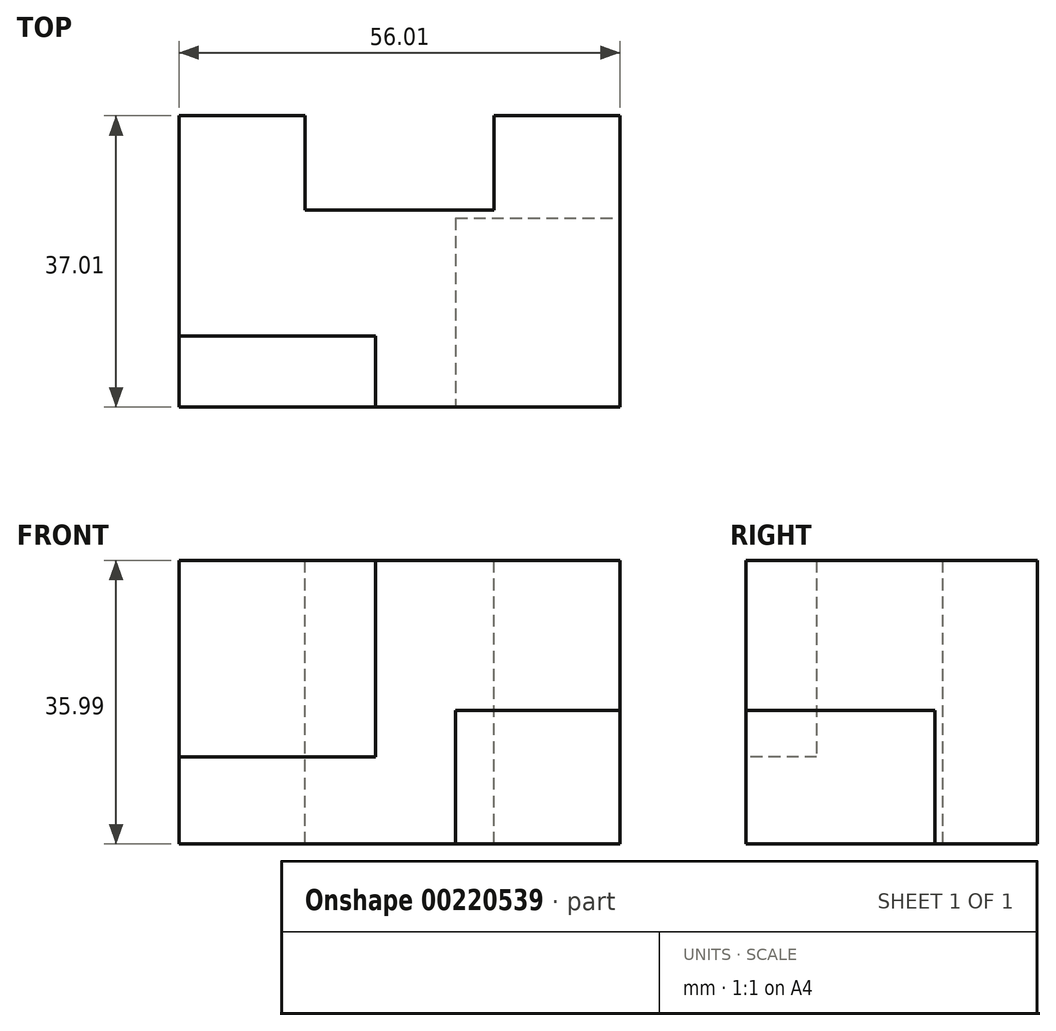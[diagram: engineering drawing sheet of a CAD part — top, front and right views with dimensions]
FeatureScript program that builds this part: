
annotation { "Feature Type Name" : "Feature", "Feature Type Description" : "" }
export const myFeature = defineFeature(function(context is Context, id is Id, definition is map)
    precondition{}
    {
        {
            var Q0;
            Q0=qCreatedBy(makeId("Top.planeOp"),FACE);
            var sketch = newSketch(context, id + "F0", { "sketchPlane" : qUnion([Q0])});
            skLineSegment(sketch, "E0.bottom", {"start": v(0, 0) * mm, "end": v(56, 0) * mm});
            skLineSegment(sketch, "E0.top", {"start": v(0, 37) * mm, "end": v(56, 37) * mm});
            skLineSegment(sketch, "E0.left", {"start": v(0, 0) * mm, "end": v(0, 37) * mm});
            skLineSegment(sketch, "E0.right", {"start": v(56, 0) * mm, "end": v(56, 37) * mm});
            skSolve(sketch);
        }
        {
            var Q0;
            Q0=makeQuery(id+"F0.imprint","IMPRINT",FACE,{"disambiguationData":[TD([[makeQuery(id+"F0.imprint","IMPRINT",EDGE,{"derivedFrom":sQuery(id+"F0.wireOp",EDGE,"E0.bottom")}),1.0]])]});
            extrude(context, id + "F1", {"entities" : qUnion([Q0]), "depth" : 36 * mm});
        }
        {
            var Q0;
            Q0=makeQuery(id+"F1.opExtrude","CAP_FACE",FACE,{"disambiguationData":[OSD([sQuery(id+"F0.wireOp",EDGE,"E0.bottom"),sQuery(id+"F0.wireOp",EDGE,"E0.top"),sQuery(id+"F0.wireOp",EDGE,"E0.left"),sQuery(id+"F0.wireOp",EDGE,"E0.right")])],"isStart":false});
            var sketch = newSketch(context, id + "F2", { "sketchPlane" : qUnion([Q0])});
            skLineSegment(sketch, "E1", {"start": v(16, 37) * mm, "end": v(16, 25.02) * mm});
            skLineSegment(sketch, "E2", {"start": v(16, 25.02) * mm, "end": v(40, 25.02) * mm});
            skLineSegment(sketch, "E3", {"start": v(40, 25.02) * mm, "end": v(40, 37) * mm});
            skLineSegment(sketch, "E4", {"start": v(0, 13.38) * mm, "end": v(56, 13.38) * mm, "construction": true});
            skLineSegment(sketch, "E5", {"start": v(28, 13.38) * mm, "end": v(28, 45.5) * mm, "construction": true});
            skPoint(sketch, "E5.endSnap0", {"position": v(28, 37) * mm});
            skLineSegment(sketch, "E6", {"start": v(16, 31.01) * mm, "end": v(0, 31.01) * mm, "construction": true});
            skSolve(sketch);
        }
        {
            var Q0;
            {var subQ0=sQuery(id+"F2.wireOp",EDGE,"E1");Q0=makeQuery(id+"F2.imprint","IMPRINT",FACE,{"disambiguationData":[TD([[makeQuery(id+"F2.imprint","IMPRINT",EDGE,{"derivedFrom":subQ0}),1.0]])]});}
            extrude(context, id + "F3", {"entities" : qUnion([Q0]), "operationType" : NewBodyOperationType.REMOVE, "oppositeDirection" : true, "depth" : 81.53 * mm});
        }
        {
            var Q0;
            Q0=makeQuery(id+"F1.opExtrude","SWEPT_FACE",FACE,{"disambiguationData":[OSD([sQuery(id+"F0.wireOp",EDGE,"E0.bottom")])]});
            var sketch = newSketch(context, id + "F4", { "sketchPlane" : qUnion([Q0])});
            skLineSegment(sketch, "E7.bottom", {"start": v(0, 36) * mm, "end": v(24.97, 36) * mm});
            skLineSegment(sketch, "E7.top", {"start": v(0, 11.05) * mm, "end": v(24.97, 11.05) * mm});
            skLineSegment(sketch, "E7.left", {"start": v(0, 36) * mm, "end": v(0, 11.05) * mm});
            skLineSegment(sketch, "E7.right", {"start": v(24.97, 36) * mm, "end": v(24.97, 11.05) * mm});
            skSolve(sketch);
        }
        {
            var Q0;
            Q0=makeQuery(id+"F4.imprint","IMPRINT",FACE,{"disambiguationData":[TD([[makeQuery(id+"F4.imprint","IMPRINT",EDGE,{"derivedFrom":sQuery(id+"F4.wireOp",EDGE,"E7.bottom")}),-1.0]])]});
            extrude(context, id + "F5", {"entities" : qUnion([Q0]), "operationType" : NewBodyOperationType.REMOVE, "oppositeDirection" : true, "depth" : 9 * mm});
        }
        {
            var Q0;
            Q0=makeQuery(id+"F1.opExtrude","SWEPT_FACE",FACE,{"disambiguationData":[OSD([sQuery(id+"F0.wireOp",EDGE,"E0.bottom")])]});
            var sketch = newSketch(context, id + "F6", { "sketchPlane" : qUnion([Q0])});
            skLineSegment(sketch, "E8.bottom", {"start": v(56, 0) * mm, "end": v(35.15, 0) * mm});
            skLineSegment(sketch, "E8.top", {"start": v(56, 16.94) * mm, "end": v(35.15, 16.94) * mm});
            skLineSegment(sketch, "E8.left", {"start": v(56, 0) * mm, "end": v(56, 16.94) * mm});
            skLineSegment(sketch, "E8.right", {"start": v(35.15, 0) * mm, "end": v(35.15, 16.94) * mm});
            skSolve(sketch);
        }
        {
            var Q0;
            Q0=makeQuery(id+"F6.imprint","IMPRINT",FACE,{"disambiguationData":[TD([[makeQuery(id+"F6.imprint","IMPRINT",EDGE,{"derivedFrom":sQuery(id+"F6.wireOp",EDGE,"E8.bottom")}),1.0]])]});
            extrude(context, id + "F7", {"entities" : qUnion([Q0]), "operationType" : NewBodyOperationType.REMOVE, "oppositeDirection" : true, "depth" : 24 * mm});
        }
    });
